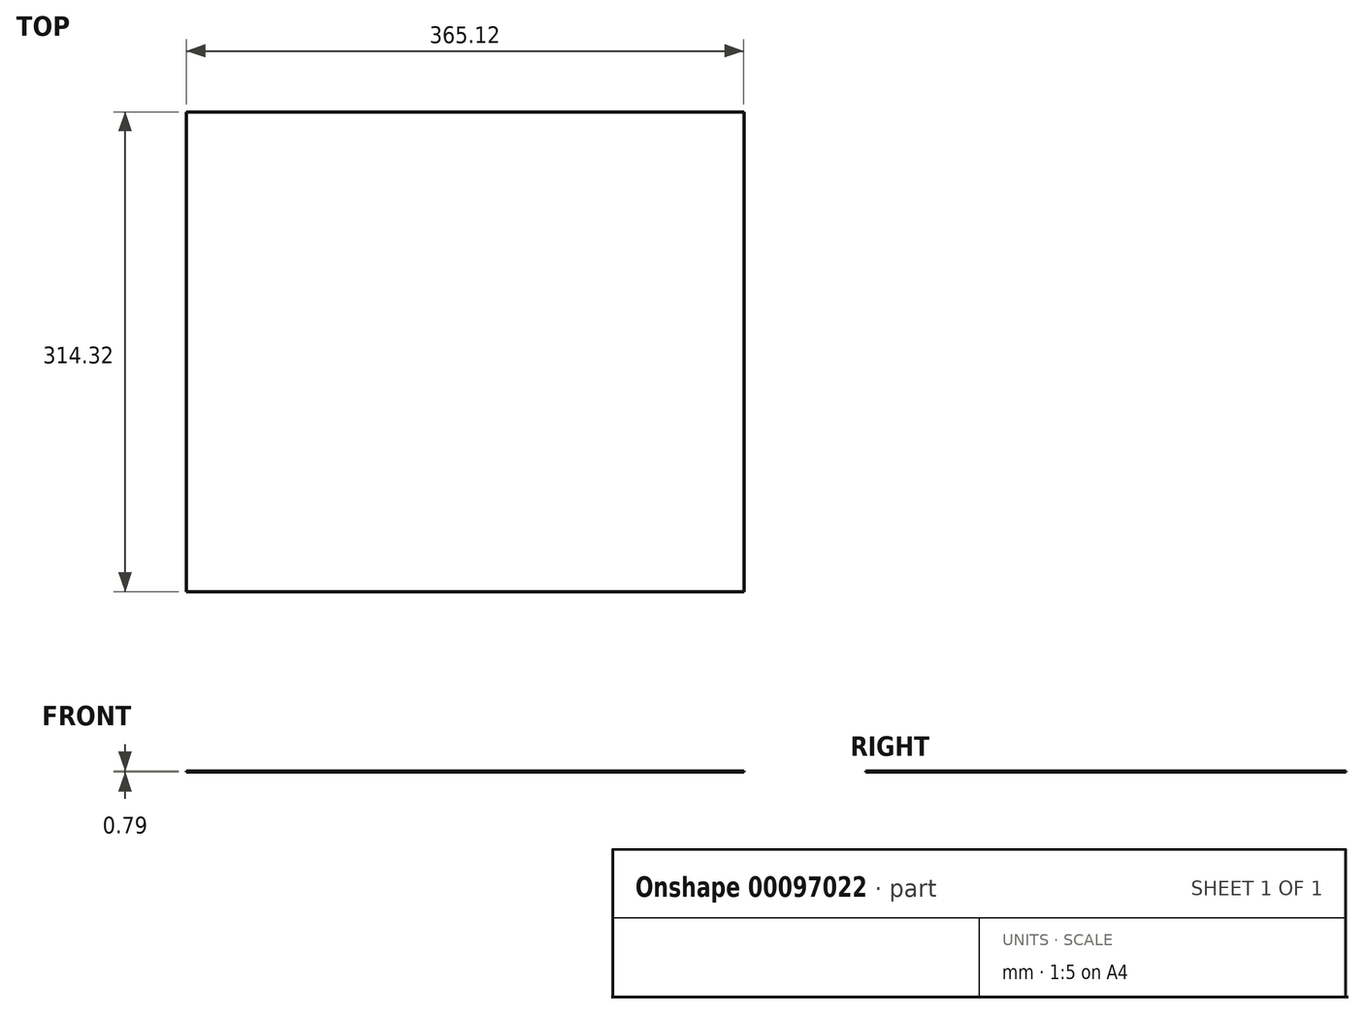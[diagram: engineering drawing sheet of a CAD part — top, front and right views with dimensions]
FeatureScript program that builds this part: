
annotation { "Feature Type Name" : "Feature", "Feature Type Description" : "" }
export const myFeature = defineFeature(function(context is Context, id is Id, definition is map)
    precondition{}
    {
        {
            var Q0;
            Q0=qCreatedBy(makeId("Top.planeOp"),FACE);
            var sketch = newSketch(context, id + "F0", { "sketchPlane" : qUnion([Q0])});
            skLineSegment(sketch, "E0.bottom", {"start": v(-182.56, 157.16) * mm, "end": v(182.56, 157.16) * mm});
            skLineSegment(sketch, "E0.top", {"start": v(-182.56, -157.16) * mm, "end": v(182.56, -157.16) * mm});
            skLineSegment(sketch, "E0.left", {"start": v(-182.56, 157.16) * mm, "end": v(-182.56, -157.16) * mm});
            skLineSegment(sketch, "E0.right", {"start": v(182.56, 157.16) * mm, "end": v(182.56, -157.16) * mm});
            skPoint(sketch, "E0.middle", {"position": v(0, 0) * mm});
            skSolve(sketch);
        }
        {
            var Q0;
            Q0 = qSketchRegion(id + "F0", true);
            extrude(context, id + "F1", {"entities" : qUnion([Q0]), "depth" : 0.8 * mm});
        }
    });
